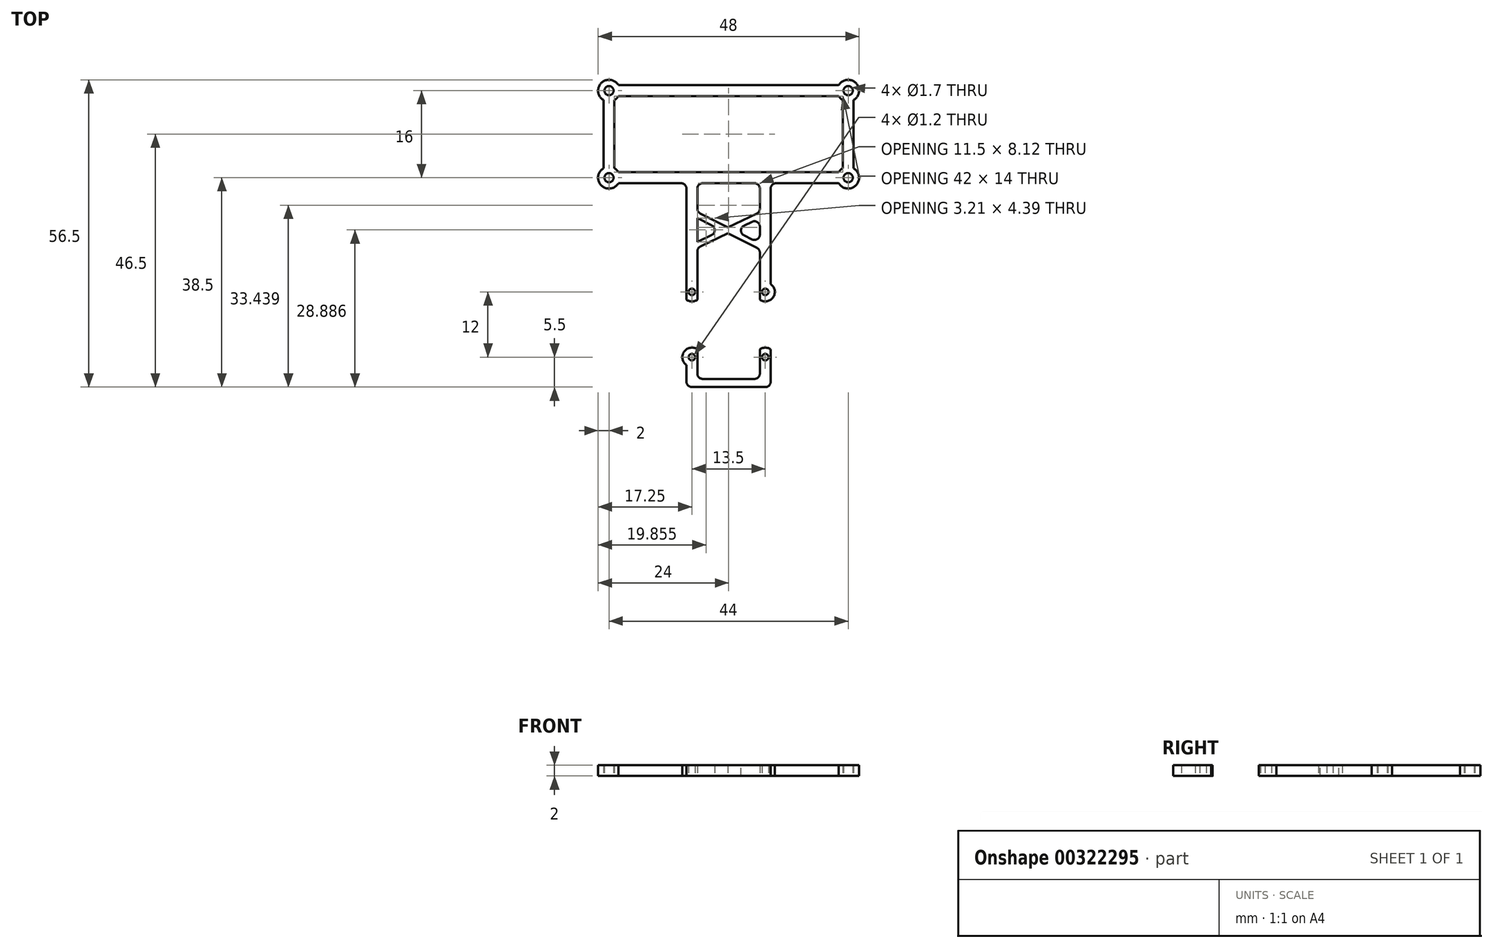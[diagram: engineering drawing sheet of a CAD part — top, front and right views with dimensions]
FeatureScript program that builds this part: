
annotation { "Feature Type Name" : "Feature", "Feature Type Description" : "" }
export const myFeature = defineFeature(function(context is Context, id is Id, definition is map)
    precondition{}
    {
        {
            var Q0;
            Q0=qCreatedBy(makeId("Top.planeOp"),FACE);
            var sketch = newSketch(context, id + "F0", { "sketchPlane" : qUnion([Q0])});
            skLineSegment(sketch, "E0.bottom", {"start": v(-22, 8) * mm, "end": v(22, 8) * mm, "construction": true});
            skLineSegment(sketch, "E0.top", {"start": v(-22, -8) * mm, "end": v(22, -8) * mm, "construction": true});
            skLineSegment(sketch, "E0.left", {"start": v(-22, 8) * mm, "end": v(-22, -8) * mm, "construction": true});
            skLineSegment(sketch, "E0.right", {"start": v(22, 8) * mm, "end": v(22, -8) * mm, "construction": true});
            skPoint(sketch, "E0.middle", {"position": v(0, 0) * mm});
            skCircle(sketch, "E1", {"center": v(-22, -8) * mm, "radius": 0.85 * mm});
            skCircle(sketch, "E2", {"center": v(22, -8) * mm, "radius": 0.85 * mm});
            skCircle(sketch, "E3", {"center": v(22, 8) * mm, "radius": 0.85 * mm});
            skCircle(sketch, "E4", {"center": v(-22, 8) * mm, "radius": 0.85 * mm});
            skLineSegment(sketch, "E5.bottom", {"start": v(-6.75, -41) * mm, "end": v(6.75, -41) * mm, "construction": true});
            skLineSegment(sketch, "E5.top", {"start": v(-6.75, -29) * mm, "end": v(6.75, -29) * mm, "construction": true});
            skLineSegment(sketch, "E5.left", {"start": v(-6.75, -41) * mm, "end": v(-6.75, -29) * mm, "construction": true});
            skLineSegment(sketch, "E5.right", {"start": v(6.75, -41) * mm, "end": v(6.75, -29) * mm, "construction": true});
            skPoint(sketch, "E5.middle", {"position": v(0, -35) * mm});
            skCircle(sketch, "E6", {"center": v(-6.75, -29) * mm, "radius": 0.6 * mm});
            skCircle(sketch, "E7", {"center": v(6.75, -29) * mm, "radius": 0.6 * mm});
            skCircle(sketch, "E8", {"center": v(6.75, -41) * mm, "radius": 0.6 * mm});
            skCircle(sketch, "E9", {"center": v(-6.75, -41) * mm, "radius": 0.6 * mm});
            skCircle(sketch, "E10", {"center": v(-22, 8) * mm, "radius": 2 * mm});
            skCircle(sketch, "E11", {"center": v(-22, -8) * mm, "radius": 2 * mm});
            skCircle(sketch, "E12", {"center": v(22, -8) * mm, "radius": 2 * mm});
            skCircle(sketch, "E13", {"center": v(22, 8) * mm, "radius": 2 * mm});
            skLineSegment(sketch, "E14.bottom", {"start": v(-23, 9) * mm, "end": v(23, 9) * mm});
            skLineSegment(sketch, "E14.top", {"start": v(-23, -9) * mm, "end": v(23, -9) * mm});
            skLineSegment(sketch, "E14.left", {"start": v(-23, 9) * mm, "end": v(-23, -9) * mm});
            skLineSegment(sketch, "E14.right", {"start": v(23, 9) * mm, "end": v(23, -9) * mm});
            skLineSegment(sketch, "E15.bottom", {"start": v(-21, -7) * mm, "end": v(21, -7) * mm});
            skLineSegment(sketch, "E15.top", {"start": v(-21, 7) * mm, "end": v(21, 7) * mm});
            skLineSegment(sketch, "E15.left", {"start": v(-21, -7) * mm, "end": v(-21, 7) * mm});
            skLineSegment(sketch, "E15.right", {"start": v(21, -7) * mm, "end": v(21, 7) * mm});
            skLineSegment(sketch, "E16", {"start": v(-7.75, -9) * mm, "end": v(-7.75, -46.5) * mm});
            skLineSegment(sketch, "E17", {"start": v(-5.75, -9) * mm, "end": v(-5.75, -45) * mm});
            skLineSegment(sketch, "E18", {"start": v(5.75, -9) * mm, "end": v(5.75, -45) * mm});
            skLineSegment(sketch, "E19", {"start": v(7.75, -9) * mm, "end": v(7.75, -46.5) * mm});
            skLineSegment(sketch, "E20", {"start": v(-5.75, -45) * mm, "end": v(5.75, -45) * mm});
            skLineSegment(sketch, "E21", {"start": v(-7.75, -46.5) * mm, "end": v(7.75, -46.5) * mm});
            skCircle(sketch, "E22", {"center": v(-6.75, -29) * mm, "radius": 1.75 * mm});
            skCircle(sketch, "E23", {"center": v(-6.75, -41) * mm, "radius": 1.75 * mm});
            skCircle(sketch, "E24", {"center": v(6.75, -41) * mm, "radius": 1.75 * mm});
            skCircle(sketch, "E25", {"center": v(6.75, -29) * mm, "radius": 1.75 * mm});
            skLineSegment(sketch, "E26", {"start": v(0, -0.2) * mm, "end": v(0, -22.77) * mm, "construction": true});
            skPoint(sketch, "E27.middle", {"position": v(0, -17.66) * mm});
            skLineSegment(sketch, "E28", {"start": v(5.75, -20.07) * mm, "end": v(-5.75, -14.3) * mm});
            skLineSegment(sketch, "E29", {"start": v(-5.75, -15.42) * mm, "end": v(5.75, -21.2) * mm});
            skLineSegment(sketch, "E30", {"start": v(-5.75, -19.81) * mm, "end": v(5.75, -14.31) * mm});
            skLineSegment(sketch, "E31", {"start": v(-5.75, -20.92) * mm, "end": v(5.75, -15.42) * mm});
            skSolve(sketch);
        }
        {
            var Q0;
            {var subQ2=sQuery(id+"F0.wireOp",EDGE,"TIqQSg9g-Fv3U-Gjd0-SPKQ-YSADvdxvNZ0G.left");Q0=makeQuery(id+"F0.imprint","IMPRINT",FACE,{"disambiguationData":[TD([[makeQuery(id+"F0.imprint","IMPRINT",EDGE,{"derivedFrom":subQ2}),-1.0]])]});}
            var Q1;
            Q1=makeQuery(id+"F0.imprint","IMPRINT",FACE,{"disambiguationData":[TD([[makeQuery(id+"F0.imprint","IMPRINT",EDGE,{"derivedFrom":sQuery(id+"F0.wireOp",EDGE,"E6")}),-1.0]])]});
            var Q2;
            {var subQ0=sQuery(id+"F0.wireOp",EDGE,"E22");var subQ1=sQuery(id+"F0.wireOp",EDGE,"E16");var subQ2=makeQuery(id+"F0.imprint","INTERSECT",VERTEX,{"disambiguationData":[OD(0.0)],"derivedFrom":[subQ1,subQ0]});Q2=makeQuery(id+"F0.imprint","IMPRINT",FACE,{"disambiguationData":[TD([[makeQuery(id+"F0.imprint","IMPRINT",EDGE,{"disambiguationData":[TD([[subQ2,-1.0]])],"derivedFrom":subQ1}),-1.0]])]});}
            var Q3;
            {var subQ0=sQuery(id+"F0.wireOp",EDGE,"E22");var subQ1=sQuery(id+"F0.wireOp",EDGE,"E16");var subQ2=makeQuery(id+"F0.imprint","INTERSECT",VERTEX,{"disambiguationData":[OD(1.0)],"derivedFrom":[subQ1,subQ0]});Q3=makeQuery(id+"F0.imprint","IMPRINT",FACE,{"disambiguationData":[TD([[makeQuery(id+"F0.imprint","IMPRINT",EDGE,{"disambiguationData":[TD([[subQ2,-1.0]])],"derivedFrom":subQ1}),1.0]])]});}
            var Q4;
            {var subQ0=sQuery(id+"F0.wireOp",EDGE,"E23");var subQ1=sQuery(id+"F0.wireOp",EDGE,"E16");var subQ2=makeQuery(id+"F0.imprint","INTERSECT",VERTEX,{"disambiguationData":[OD(0.0)],"derivedFrom":[subQ1,subQ0]});Q4=makeQuery(id+"F0.imprint","IMPRINT",FACE,{"disambiguationData":[TD([[makeQuery(id+"F0.imprint","IMPRINT",EDGE,{"disambiguationData":[TD([[subQ2,-1.0]])],"derivedFrom":subQ1}),-1.0]])]});}
            var Q5;
            Q5=makeQuery(id+"F0.imprint","IMPRINT",FACE,{"disambiguationData":[TD([[makeQuery(id+"F0.imprint","IMPRINT",EDGE,{"derivedFrom":sQuery(id+"F0.wireOp",EDGE,"E9")}),-1.0]])]});
            var Q6;
            {var subQ4=sQuery(id+"F0.wireOp",EDGE,"E20");Q6=makeQuery(id+"F0.imprint","IMPRINT",FACE,{"disambiguationData":[TD([[makeQuery(id+"F0.imprint","IMPRINT",EDGE,{"derivedFrom":subQ4}),-1.0]])]});}
            var Q7;
            Q7=makeQuery(id+"F0.imprint","IMPRINT",FACE,{"disambiguationData":[TD([[makeQuery(id+"F0.imprint","IMPRINT",EDGE,{"derivedFrom":sQuery(id+"F0.wireOp",EDGE,"E7")}),-1.0]])]});
            var Q8;
            {var subQ0=sQuery(id+"F0.wireOp",EDGE,"E25");var subQ1=sQuery(id+"F0.wireOp",EDGE,"E19");var subQ2=makeQuery(id+"F0.imprint","INTERSECT",VERTEX,{"disambiguationData":[OD(0.0)],"derivedFrom":[subQ1,subQ0]});Q8=makeQuery(id+"F0.imprint","IMPRINT",FACE,{"disambiguationData":[TD([[makeQuery(id+"F0.imprint","IMPRINT",EDGE,{"disambiguationData":[TD([[subQ2,-1.0]])],"derivedFrom":subQ1}),1.0]])]});}
            var Q9;
            {var subQ0=sQuery(id+"F0.wireOp",EDGE,"E25");var subQ1=sQuery(id+"F0.wireOp",EDGE,"E18");var subQ2=makeQuery(id+"F0.imprint","INTERSECT",VERTEX,{"disambiguationData":[OD(1.0)],"derivedFrom":[subQ1,subQ0]});Q9=makeQuery(id+"F0.imprint","IMPRINT",FACE,{"disambiguationData":[TD([[makeQuery(id+"F0.imprint","IMPRINT",EDGE,{"disambiguationData":[TD([[subQ2,-1.0]])],"derivedFrom":subQ1}),1.0]])]});}
            var Q10;
            Q10=makeQuery(id+"F0.imprint","IMPRINT",FACE,{"disambiguationData":[TD([[makeQuery(id+"F0.imprint","IMPRINT",EDGE,{"derivedFrom":sQuery(id+"F0.wireOp",EDGE,"E8")}),-1.0]])]});
            var Q11;
            {var subQ0=sQuery(id+"F0.wireOp",EDGE,"E24");var subQ1=sQuery(id+"F0.wireOp",EDGE,"E19");var subQ2=makeQuery(id+"F0.imprint","INTERSECT",VERTEX,{"disambiguationData":[OD(0.0)],"derivedFrom":[subQ1,subQ0]});Q11=makeQuery(id+"F0.imprint","IMPRINT",FACE,{"disambiguationData":[TD([[makeQuery(id+"F0.imprint","IMPRINT",EDGE,{"disambiguationData":[TD([[subQ2,-1.0]])],"derivedFrom":subQ1}),1.0]])]});}
            var Q12;
            {var subQ2=sQuery(id+"F0.wireOp",EDGE,"TIqQSg9g-Fv3U-Gjd0-SPKQ-YSADvdxvNZ0G.right");Q12=makeQuery(id+"F0.imprint","IMPRINT",FACE,{"disambiguationData":[TD([[makeQuery(id+"F0.imprint","IMPRINT",EDGE,{"derivedFrom":subQ2}),1.0]])]});}
            var Q13;
            {var subQ0=sQuery(id+"F0.wireOp",EDGE,"E14.top");var subQ7=sQuery(id+"F0.wireOp",EDGE,"E11");var subQ8=makeQuery(id+"F0.imprint","INTERSECT",VERTEX,{"derivedFrom":[subQ7,subQ0]});Q13=makeQuery(id+"F0.imprint","IMPRINT",FACE,{"disambiguationData":[TD([[makeQuery(id+"F0.imprint","IMPRINT",EDGE,{"disambiguationData":[TD([[subQ8,-1.0]])],"derivedFrom":subQ7}),-1.0]])]});}
            var Q14;
            {var subQ0=sQuery(id+"F0.wireOp",EDGE,"E14.right");var subQ1=sQuery(id+"F0.wireOp",EDGE,"E12");var subQ2=makeQuery(id+"F0.imprint","INTERSECT",VERTEX,{"derivedFrom":[subQ1,subQ0]});Q14=makeQuery(id+"F0.imprint","IMPRINT",FACE,{"disambiguationData":[TD([[makeQuery(id+"F0.imprint","IMPRINT",EDGE,{"disambiguationData":[TD([[subQ2,1.0]])],"derivedFrom":subQ1}),1.0]])]});}
            var Q15;
            Q15=makeQuery(id+"F0.imprint","IMPRINT",FACE,{"disambiguationData":[TD([[makeQuery(id+"F0.imprint","IMPRINT",EDGE,{"derivedFrom":sQuery(id+"F0.wireOp",EDGE,"E2")}),-1.0]])]});
            var Q16;
            {var subQ0=sQuery(id+"F0.wireOp",EDGE,"E14.right");var subQ1=sQuery(id+"F0.wireOp",EDGE,"E12");var subQ2=makeQuery(id+"F0.imprint","INTERSECT",VERTEX,{"derivedFrom":[subQ1,subQ0]});Q16=makeQuery(id+"F0.imprint","IMPRINT",FACE,{"disambiguationData":[TD([[makeQuery(id+"F0.imprint","IMPRINT",EDGE,{"disambiguationData":[TD([[subQ2,-1.0]])],"derivedFrom":subQ1}),-1.0]])]});}
            var Q17;
            {var subQ0=sQuery(id+"F0.wireOp",EDGE,"E15.right");var subQ1=sQuery(id+"F0.wireOp",EDGE,"E12");var subQ2=makeQuery(id+"F0.imprint","INTERSECT",VERTEX,{"derivedFrom":[subQ1,subQ0]});Q17=makeQuery(id+"F0.imprint","IMPRINT",FACE,{"disambiguationData":[TD([[makeQuery(id+"F0.imprint","IMPRINT",EDGE,{"disambiguationData":[TD([[subQ2,-1.0]])],"derivedFrom":subQ1}),1.0]])]});}
            var Q18;
            {var subQ0=sQuery(id+"F0.wireOp",EDGE,"E15.top");var subQ1=sQuery(id+"F0.wireOp",EDGE,"E13");var subQ2=makeQuery(id+"F0.imprint","INTERSECT",VERTEX,{"derivedFrom":[subQ1,subQ0]});Q18=makeQuery(id+"F0.imprint","IMPRINT",FACE,{"disambiguationData":[TD([[makeQuery(id+"F0.imprint","IMPRINT",EDGE,{"disambiguationData":[TD([[subQ2,-1.0]])],"derivedFrom":subQ1}),1.0]])]});}
            var Q19;
            Q19=makeQuery(id+"F0.imprint","IMPRINT",FACE,{"disambiguationData":[TD([[makeQuery(id+"F0.imprint","IMPRINT",EDGE,{"derivedFrom":sQuery(id+"F0.wireOp",EDGE,"E3")}),-1.0]])]});
            var Q20;
            {var subQ0=sQuery(id+"F0.wireOp",EDGE,"E14.bottom");var subQ1=sQuery(id+"F0.wireOp",EDGE,"E13");var subQ2=makeQuery(id+"F0.imprint","INTERSECT",VERTEX,{"derivedFrom":[subQ1,subQ0]});Q20=makeQuery(id+"F0.imprint","IMPRINT",FACE,{"disambiguationData":[TD([[makeQuery(id+"F0.imprint","IMPRINT",EDGE,{"disambiguationData":[TD([[subQ2,1.0]])],"derivedFrom":subQ1}),1.0]])]});}
            var Q21;
            {var subQ0=sQuery(id+"F0.wireOp",EDGE,"E14.bottom");var subQ1=sQuery(id+"F0.wireOp",EDGE,"E10");var subQ2=makeQuery(id+"F0.imprint","INTERSECT",VERTEX,{"derivedFrom":[subQ1,subQ0]});Q21=makeQuery(id+"F0.imprint","IMPRINT",FACE,{"disambiguationData":[TD([[makeQuery(id+"F0.imprint","IMPRINT",EDGE,{"disambiguationData":[TD([[subQ2,1.0]])],"derivedFrom":subQ1}),-1.0]])]});}
            var Q22;
            Q22=makeQuery(id+"F0.imprint","IMPRINT",FACE,{"disambiguationData":[TD([[makeQuery(id+"F0.imprint","IMPRINT",EDGE,{"derivedFrom":sQuery(id+"F0.wireOp",EDGE,"E1")}),-1.0]])]});
            var Q23;
            {var subQ0=sQuery(id+"F0.wireOp",EDGE,"E14.left");var subQ1=sQuery(id+"F0.wireOp",EDGE,"E11");var subQ2=makeQuery(id+"F0.imprint","INTERSECT",VERTEX,{"derivedFrom":[subQ1,subQ0]});Q23=makeQuery(id+"F0.imprint","IMPRINT",FACE,{"disambiguationData":[TD([[makeQuery(id+"F0.imprint","IMPRINT",EDGE,{"disambiguationData":[TD([[subQ2,-1.0]])],"derivedFrom":subQ1}),1.0]])]});}
            var Q24;
            {var subQ0=sQuery(id+"F0.wireOp",EDGE,"E15.left");var subQ1=sQuery(id+"F0.wireOp",EDGE,"E11");var subQ2=makeQuery(id+"F0.imprint","INTERSECT",VERTEX,{"derivedFrom":[subQ1,subQ0]});Q24=makeQuery(id+"F0.imprint","IMPRINT",FACE,{"disambiguationData":[TD([[makeQuery(id+"F0.imprint","IMPRINT",EDGE,{"disambiguationData":[TD([[subQ2,1.0]])],"derivedFrom":subQ1}),1.0]])]});}
            var Q25;
            {var subQ0=sQuery(id+"F0.wireOp",EDGE,"E14.left");var subQ1=sQuery(id+"F0.wireOp",EDGE,"E10");var subQ2=makeQuery(id+"F0.imprint","INTERSECT",VERTEX,{"derivedFrom":[subQ1,subQ0]});Q25=makeQuery(id+"F0.imprint","IMPRINT",FACE,{"disambiguationData":[TD([[makeQuery(id+"F0.imprint","IMPRINT",EDGE,{"disambiguationData":[TD([[subQ2,1.0]])],"derivedFrom":subQ1}),1.0]])]});}
            var Q26;
            Q26=makeQuery(id+"F0.imprint","IMPRINT",FACE,{"disambiguationData":[TD([[makeQuery(id+"F0.imprint","IMPRINT",EDGE,{"derivedFrom":sQuery(id+"F0.wireOp",EDGE,"E4")}),-1.0]])]});
            var Q27;
            {var subQ0=sQuery(id+"F0.wireOp",EDGE,"E15.left");var subQ1=sQuery(id+"F0.wireOp",EDGE,"E10");var subQ2=makeQuery(id+"F0.imprint","INTERSECT",VERTEX,{"derivedFrom":[subQ1,subQ0]});Q27=makeQuery(id+"F0.imprint","IMPRINT",FACE,{"disambiguationData":[TD([[makeQuery(id+"F0.imprint","IMPRINT",EDGE,{"disambiguationData":[TD([[subQ2,-1.0]])],"derivedFrom":subQ1}),1.0]])]});}
            var Q28;
            {var subQ0=sQuery(id+"F0.wireOp",EDGE,"E14.left");var subQ1=sQuery(id+"F0.wireOp",EDGE,"E10");var subQ2=makeQuery(id+"F0.imprint","INTERSECT",VERTEX,{"derivedFrom":[subQ1,subQ0]});Q28=makeQuery(id+"F0.imprint","IMPRINT",FACE,{"disambiguationData":[TD([[makeQuery(id+"F0.imprint","IMPRINT",EDGE,{"disambiguationData":[TD([[subQ2,-1.0]])],"derivedFrom":subQ1}),-1.0]])]});}
            var Q29;
            {var subQ0=sQuery(id+"F0.wireOp",EDGE,"E18");var subQ4=sQuery(id+"F0.wireOp",EDGE,"E14.top");var subQ5=makeQuery(id+"F0.imprint","INTERSECT",VERTEX,{"derivedFrom":[subQ4,subQ0]});Q29=makeQuery(id+"F0.imprint","IMPRINT",FACE,{"disambiguationData":[TD([[makeQuery(id+"F0.imprint","IMPRINT",EDGE,{"disambiguationData":[TD([[subQ5,-1.0]])],"derivedFrom":subQ4}),-1.0]])]});}
            var Q30;
            {var subQ0=sQuery(id+"F0.wireOp",EDGE,"E28");var subQ1=sQuery(id+"F0.wireOp",EDGE,"E18");var subQ2=makeQuery(id+"F0.imprint","INTERSECT",VERTEX,{"derivedFrom":[subQ1,subQ0]});Q30=makeQuery(id+"F0.imprint","IMPRINT",FACE,{"disambiguationData":[TD([[makeQuery(id+"F0.imprint","IMPRINT",EDGE,{"disambiguationData":[TD([[subQ2,-1.0]])],"derivedFrom":subQ1}),-1.0]])]});}
            var Q31;
            {var subQ0=sQuery(id+"F0.wireOp",EDGE,"E30");var subQ1=sQuery(id+"F0.wireOp",EDGE,"E18");var subQ2=makeQuery(id+"F0.imprint","INTERSECT",VERTEX,{"derivedFrom":[subQ1,subQ0]});Q31=makeQuery(id+"F0.imprint","IMPRINT",FACE,{"disambiguationData":[TD([[makeQuery(id+"F0.imprint","IMPRINT",EDGE,{"disambiguationData":[TD([[subQ2,-1.0]])],"derivedFrom":subQ1}),-1.0]])]});}
            var Q32;
            {var subQ0=sQuery(id+"F0.wireOp",EDGE,"E31");var subQ1=sQuery(id+"F0.wireOp",EDGE,"E28");var subQ2=makeQuery(id+"F0.imprint","INTERSECT",VERTEX,{"derivedFrom":[subQ1,subQ0]});Q32=makeQuery(id+"F0.imprint","IMPRINT",FACE,{"disambiguationData":[TD([[makeQuery(id+"F0.imprint","IMPRINT",EDGE,{"disambiguationData":[TD([[subQ2,-1.0]])],"derivedFrom":subQ1}),1.0]])]});}
            var Q33;
            {var subQ0=sQuery(id+"F0.wireOp",EDGE,"E30");var subQ1=sQuery(id+"F0.wireOp",EDGE,"E17");var subQ2=makeQuery(id+"F0.imprint","INTERSECT",VERTEX,{"derivedFrom":[subQ1,subQ0]});Q33=makeQuery(id+"F0.imprint","IMPRINT",FACE,{"disambiguationData":[TD([[makeQuery(id+"F0.imprint","IMPRINT",EDGE,{"disambiguationData":[TD([[subQ2,-1.0]])],"derivedFrom":subQ1}),1.0]])]});}
            var Q34;
            {var subQ0=sQuery(id+"F0.wireOp",EDGE,"E28");var subQ1=sQuery(id+"F0.wireOp",EDGE,"E17");var subQ2=makeQuery(id+"F0.imprint","INTERSECT",VERTEX,{"derivedFrom":[subQ1,subQ0]});Q34=makeQuery(id+"F0.imprint","IMPRINT",FACE,{"disambiguationData":[TD([[makeQuery(id+"F0.imprint","IMPRINT",EDGE,{"disambiguationData":[TD([[subQ2,-1.0]])],"derivedFrom":subQ1}),1.0]])]});}
            var Q35;
            {var subQ3=sQuery(id+"F0.wireOp",EDGE,"E14.top");var subQ5=sQuery(id+"F0.wireOp",EDGE,"E16");var subQ6=makeQuery(id+"F0.imprint","INTERSECT",VERTEX,{"derivedFrom":[subQ3,subQ5]});Q35=makeQuery(id+"F0.imprint","IMPRINT",FACE,{"disambiguationData":[TD([[makeQuery(id+"F0.imprint","IMPRINT",EDGE,{"disambiguationData":[TD([[subQ6,-1.0]])],"derivedFrom":subQ3}),-1.0]])]});}
            extrude(context, id + "F1", {"entities" : qUnion([Q0, Q1, Q2, Q3, Q4, Q5, Q6, Q7, Q8, Q9, Q10, Q11, Q12, Q13, Q14, Q15, Q16, Q17, Q18, Q19, Q20, Q21, Q22, Q23, Q24, Q25, Q26, Q27, Q28, Q29, Q30, Q31, Q32, Q33, Q34, Q35]), "depth" : 2 * mm});
        }
        {
            var Q0;
            Q0=makeQuery(id+"F1.opExtrude","SWEPT_EDGE",EDGE,{"disambiguationData":[OSD([sQuery(id+"F0.wireOp",EDGE,"E16"),sQuery(id+"F0.wireOp",EDGE,"E21")])]});
            var Q1;
            Q1=makeQuery(id+"F1.opExtrude","SWEPT_EDGE",EDGE,{"disambiguationData":[OSD([sQuery(id+"F0.wireOp",EDGE,"E19"),sQuery(id+"F0.wireOp",EDGE,"E21")])]});
            var Q2;
            Q2=makeQuery(id+"F1.opExtrude","SWEPT_EDGE",EDGE,{"disambiguationData":[OSD([sQuery(id+"F0.wireOp",EDGE,"E17"),sQuery(id+"F0.wireOp",EDGE,"E20")])]});
            var Q3;
            Q3=makeQuery(id+"F1.opExtrude","SWEPT_EDGE",EDGE,{"disambiguationData":[OSD([sQuery(id+"F0.wireOp",EDGE,"E18"),sQuery(id+"F0.wireOp",EDGE,"E20")])]});
            var Q4;
            Q4=makeQuery(id+"F1.opExtrude","SWEPT_EDGE",EDGE,{"disambiguationData":[OSD([sQuery(id+"F0.wireOp",EDGE,"E17"),sQuery(id+"F0.wireOp",EDGE,"E31")])]});
            var Q5;
            Q5=makeQuery(id+"F1.opExtrude","SWEPT_EDGE",EDGE,{"disambiguationData":[OSD([sQuery(id+"F0.wireOp",EDGE,"E18"),sQuery(id+"F0.wireOp",EDGE,"E29")])]});
            var Q6;
            Q6=makeQuery(id+"F1.opExtrude","SWEPT_EDGE",EDGE,{"disambiguationData":[OSD([sQuery(id+"F0.wireOp",EDGE,"E18"),sQuery(id+"F0.wireOp",EDGE,"E28")])]});
            var Q7;
            Q7=makeQuery(id+"F1.opExtrude","SWEPT_EDGE",EDGE,{"disambiguationData":[OSD([sQuery(id+"F0.wireOp",EDGE,"E18"),sQuery(id+"F0.wireOp",EDGE,"E31")])]});
            var Q8;
            Q8=makeQuery(id+"F1.opExtrude","SWEPT_EDGE",EDGE,{"disambiguationData":[OSD([sQuery(id+"F0.wireOp",EDGE,"E28"),sQuery(id+"F0.wireOp",EDGE,"E31")])]});
            var Q9;
            Q9=makeQuery(id+"F1.opExtrude","SWEPT_EDGE",EDGE,{"disambiguationData":[OSD([sQuery(id+"F0.wireOp",EDGE,"E29"),sQuery(id+"F0.wireOp",EDGE,"E30")])]});
            var Q10;
            Q10=makeQuery(id+"F1.opExtrude","SWEPT_EDGE",EDGE,{"disambiguationData":[OSD([sQuery(id+"F0.wireOp",EDGE,"E17"),sQuery(id+"F0.wireOp",EDGE,"E28")])]});
            var Q11;
            Q11=makeQuery(id+"F1.opExtrude","SWEPT_EDGE",EDGE,{"disambiguationData":[OSD([sQuery(id+"F0.wireOp",EDGE,"E18"),sQuery(id+"F0.wireOp",EDGE,"E30")])]});
            var Q12;
            Q12=makeQuery(id+"F1.opExtrude","SWEPT_EDGE",EDGE,{"disambiguationData":[OSD([sQuery(id+"F0.wireOp",EDGE,"E14.top"),sQuery(id+"F0.wireOp",EDGE,"E18")])]});
            var Q13;
            Q13=makeQuery(id+"F1.opExtrude","SWEPT_EDGE",EDGE,{"disambiguationData":[OSD([sQuery(id+"F0.wireOp",EDGE,"E14.top"),sQuery(id+"F0.wireOp",EDGE,"E17")])]});
            var Q14;
            Q14=makeQuery(id+"F1.opExtrude","SWEPT_EDGE",EDGE,{"disambiguationData":[OSD([sQuery(id+"F0.wireOp",EDGE,"E14.top"),sQuery(id+"F0.wireOp",EDGE,"E16")])]});
            var Q15;
            Q15=makeQuery(id+"F1.opExtrude","SWEPT_EDGE",EDGE,{"disambiguationData":[OSD([sQuery(id+"F0.wireOp",EDGE,"E14.top"),sQuery(id+"F0.wireOp",EDGE,"E19")])]});
            fillet(context, id + "F2", {"entities" : qUnion([Q0, Q1, Q2, Q3, Q4, Q5, Q6, Q7, Q8, Q9, Q10, Q11, Q12, Q13, Q14, Q15]), "radius" : 1 * mm, "tangentPropagation" : true, "allowEdgeOverflow" : false});
        }
    });
